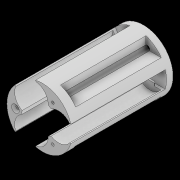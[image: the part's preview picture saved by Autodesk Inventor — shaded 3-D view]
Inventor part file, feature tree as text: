
AUTODESK INVENTOR PART (.ipt)
format: ipt  version: 2022 (Build 260153000, 153)  size: 488,448 bytes
history: native  units: mm
features: sketch x24, extrude x20, projected_geometry x10, hole x5, pattern_circular x2, chamfer x2, plane x2
ambient origin geometry x8: Origin, YZ Plane, XZ Plane, XY Plane, X Axis, Y Axis, Z Axis, Center Point
bodies: Volumenkörper1 (feature_tree)
feature tree (65):
  extrude  "Extrusion1"  Depth=8.0mm TaperAngle=0.0deg
  extrude  "Extrusion2"  Depth=30.0mm TaperAngle=360.0deg
  extrude  "Extrusion3"  Depth=4.5mm
  extrude  "Extrusion4"  Depth=4.5mm
  extrude  "Extrusion21"  Depth=2.0mm TaperAngle=0.0deg
  extrude  "Extrusion6"  Depth=6.0mm
  pattern_circular  "Runde Anordnung1"  [2 undecoded]
  extrude  "Extrusion7"  Depth=2.0mm TaperAngle=0.0deg
  extrude  "Extrusion22"  Depth=2.0mm
  extrude  "Extrusion23"  Depth=2.0mm
  hole  "Bohrung4"  [1 undecoded]
  hole  "Bohrung7"  [1 undecoded]
  hole  "Bohrung8"  [1 undecoded]
  pattern_circular  "Runde Anordnung6"  [2 undecoded]
  extrude  "Extrusion31"  TaperAngle=60.0deg  [1 undecoded]
  hole  "Bohrung9"  [1 undecoded]
  extrude  "Extrusion32"  Depth=2.0mm
  chamfer  "Fase2"  Distance=3.0mm
  hole  "Bohrung10"  [1 undecoded]
  plane  "Arbeitsebene4"
  extrude  "Extrusion33"  TaperAngle=120.0deg  [1 undecoded]
  plane  "Arbeitsebene5"
  extrude  "Extrusion34"  Depth=2.5mm
  chamfer  "Fase3"  Distance=4.0mm
  extrude  "Extrusion30"  Depth=1.5mm TaperAngle=45.0deg
  extrude  "Extrusion24"  [1 undecoded]
  extrude  "Extrusion25"  Depth=58.5mm TaperAngle=0.0deg
  extrude  "Extrusion26"  [1 undecoded]
  extrude  "Extrusion27"  Depth=58.5mm TaperAngle=0.0deg
  extrude  "Extrusion28"  Depth=1.8mm
  extrude  "Extrusion29"  Depth=1.8mm
  sketch  "Skizze1"  dims[d0=40.5mm d1=8.0mm d2=0.0mm]
  sketch  "Skizze2"  dims[d3=19.0mm d4=30.0mm d6=360.0deg]
  sketch  "Skizze3"  dims[d8=4.5mm d9=0.0mm d10=20.0mm]
  sketch  "Skizze4"  dims[d11=4.5mm d12=0.0mm d13=20.0mm]
  projected_geometry  "Projizierte Kontur1"
  projected_geometry  "Projizierte Kontur2"
  sketch  "Skizze6"  dims[d14=11.5mm d17=2.0mm d18=0.0mm]
  sketch  "Skizze7"  dims[d30=30.0mm d31=360.0deg d33=6.0mm]
  sketch  "Skizze25"  dims[d38=1.3mm d39=0.0mm]
  projected_geometry  "Projizierte Kontur6"
  sketch  "Skizze26"  dims[d40=11.0mm]
  projected_geometry  "Projizierte Kontur7"
  projected_geometry  "Projizierte Kontur8"
  projected_geometry  "Projizierte Kontur9"
  sketch  "Skizze28"  dims[d41=2.0mm d42=0.0mm]
  sketch  "Skizze29"  dims[d130=4.5mm d131=0.0mm]
  sketch  "Skizze31"  dims[d132=58.0mm d133=0.0mm]
  sketch  "Skizze32"  dims[d134=29.6mm]
  sketch  "Skizze33"  dims[d135=27.0mm]
  projected_geometry  "Projizierte Kontur11"
  projected_geometry  "Projizierte Kontur12"
  sketch  "Skizze36"  dims[d136=4.0mm d137=0.0mm]
  sketch  "Skizze37"  dims[d138=14.5mm]
  sketch  "Skizze38"  dims[d139=2.3mm d140=6.0mm d141=4.0mm d142=2.0mm d143=90.0deg d144=5.0mm d145=20.594885mm]
  sketch  "Skizze39"  dims[d153=3.0mm]
  sketch  "Skizze43"  dims[d154=11.0mm]
  sketch  "Skizze44"  dims[d155=0.0mm d156=0.0mm]
  sketch  "Skizze45"  dims[d157=1.5mm]
  sketch  "Skizze46"  dims[d158=1.5mm]
  projected_geometry  "Projizierte Kontur13"
  sketch  "Skizze47"  dims[d159=2.0mm d160=0.0mm]
  projected_geometry  "Projizierte Kontur14"
  sketch  "Skizze48"  dims[d161=10.0mm]
  sketch  "Skizze49"  dims[d162=1.0mm d163=0.0mm d165=12.0mm d166=0.5mm d167=0.0mm d168=25.0mm d169=5.0mm d170=0.5mm d171=0.0mm d172=50.0mm d173=2.0mm d174=0.0mm d175=10.0mm d176=0.0mm d184=60.0deg d185=1.8mm d186=6.0mm d187=4.0mm d188=2.0mm d189=90.0deg d190=6.3mm d191=20.594885mm d192=3.5mm d193=6.0mm d194=4.0mm d195=2.0mm d196=90.0deg d197=60.0mm d198=20.594885mm d199=20.0mm d200=240.0deg d202=2.0mm d203=3.0mm d204=0.0mm d207=10.0mm d208=120.0deg d209=2.5mm d210=5.0mm d211=6.0mm d212=4.0mm d213=2.0mm d214=90.0deg d215=80.0mm d216=0.0mm d220=4.0mm d221=0.0mm d222=1.5mm d223=2.0mm d224=45.0deg d225=3.5mm d226=6.0mm d227=4.0mm d228=2.0mm d229=90.0deg d230=60.0mm d231=20.594885mm d232=-6.0mm d233=58.5mm d234=0.0mm d235=-6.0mm d236=58.5mm d237=0.0mm d238=1.8mm d239=1.8mm d240=9.0mm d242=9.0mm d248=1.0mm d249=2.0mm d250=45.0deg d251=40.5mm d252=11.0mm d16=0.5mm d19=0.872665mm d20=0.872665mm d21=0.5mm d22=0.872665mm d52=0.5mm d53=0.872665mm d54=0.5mm d55=0.872665mm d75=0.5mm d76=0.872665mm d77=0.5mm d78=0.872665mm d93=1.0mm d94=1.0mm d95=1.0mm d96=0.15mm d97=0.25mm d98=0.375mm d99=14.3117mm d100=0.75mm d101=20.594885mm d102=0.0625mm d103=0.75mm d104=0.375mm d177=0.5mm d178=0.872665mm d179=0.5mm d180=0.872665mm d253=0.5mm d254=0.872665mm d255=0.5mm d256=0.872665mm d257=0.25mm d258=0.375mm d259=14.3117mm d260=0.75mm d261=20.594885mm d262=0.0625mm d263=0.75mm d264=0.375mm]
note: 13 required parameter values undecoded (feature->parameter linkage not recoverable at this tier; creation-order binding heuristic only, values carry confidence <= 0.55)
